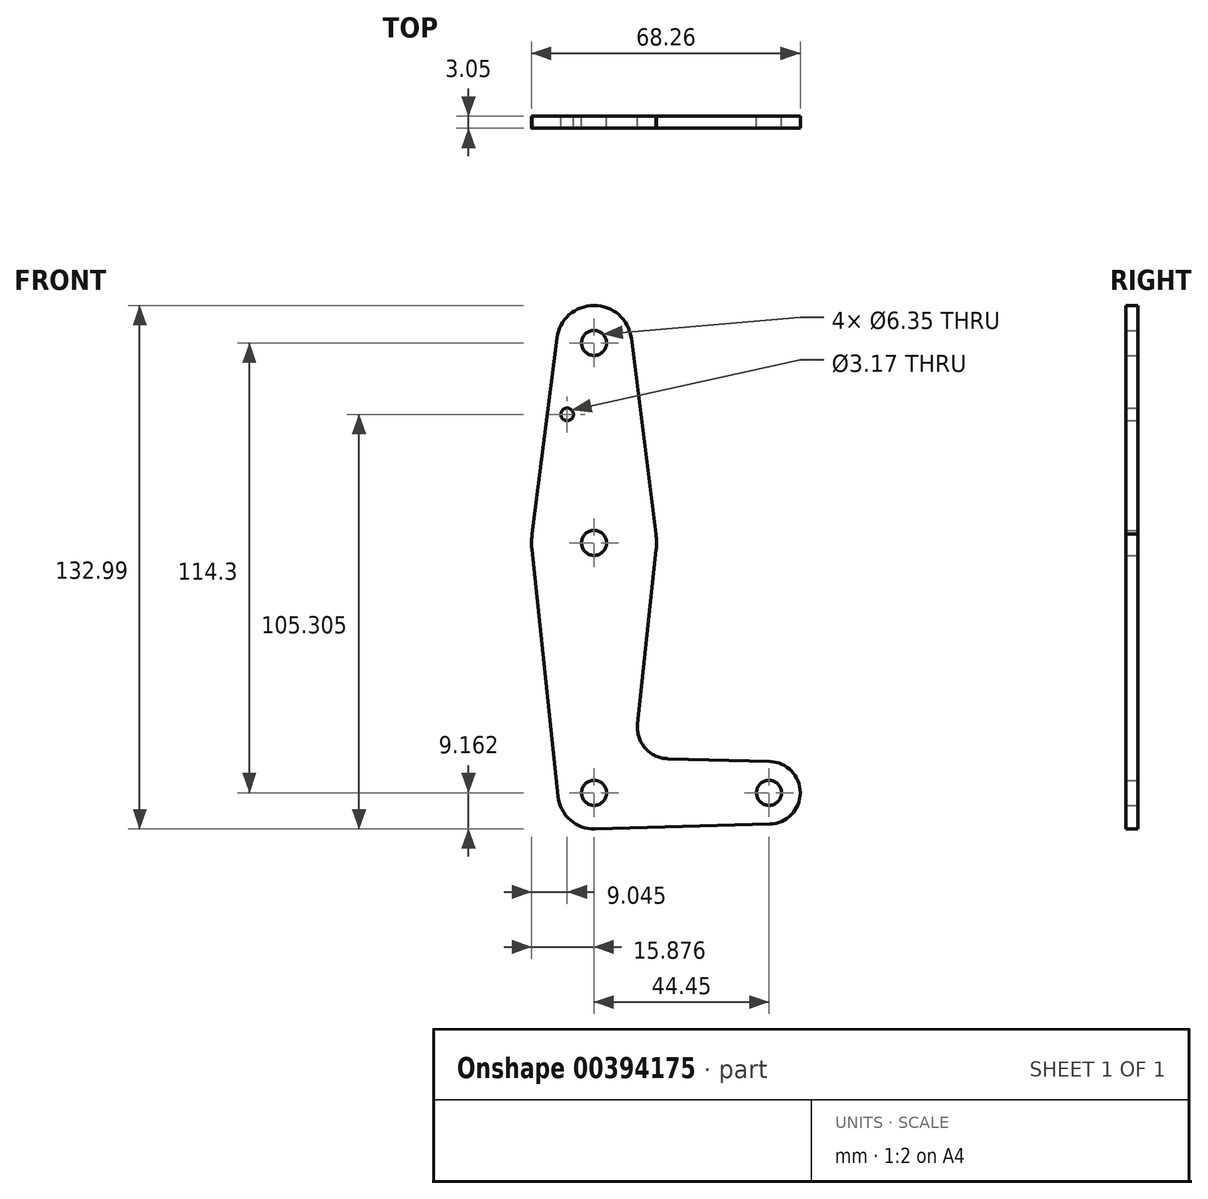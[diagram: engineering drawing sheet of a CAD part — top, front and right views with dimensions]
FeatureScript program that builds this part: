
annotation { "Feature Type Name" : "Feature", "Feature Type Description" : "" }
export const myFeature = defineFeature(function(context is Context, id is Id, definition is map)
    precondition{}
    {
        {
            var Q0;
            Q0=qCreatedBy(makeId("Front.planeOp"),FACE);
            var sketch = newSketch(context, id + "F0", { "sketchPlane" : qUnion([Q0])});
            skLineSegment(sketch, "E0", {"start": v(-37.08, 62.07) * mm, "end": v(-37.08, -52.23) * mm, "construction": true});
            skLineSegment(sketch, "E1", {"start": v(-37.08, -52.23) * mm, "end": v(7.37, -52.23) * mm, "construction": true});
            skCircle(sketch, "E2", {"center": v(-37.08, 62.07) * mm, "radius": 9.53 * mm});
            skCircle(sketch, "E3", {"center": v(-37.08, 11.27) * mm, "radius": 15.88 * mm});
            skCircle(sketch, "E4", {"center": v(-37.08, -52.23) * mm, "radius": 9.17 * mm});
            skCircle(sketch, "E5", {"center": v(7.37, -52.23) * mm, "radius": 7.94 * mm});
            skLineSegment(sketch, "E6", {"start": v(-52.87, 12.92) * mm, "end": v(-46.53, 63.26) * mm});
            skLineSegment(sketch, "E7", {"start": v(-27.63, 63.26) * mm, "end": v(-21.3, 12.92) * mm});
            skLineSegment(sketch, "E8", {"start": v(-52.87, 9.63) * mm, "end": v(-46.2, -53.2) * mm});
            skLineSegment(sketch, "E9", {"start": v(-26.01, -34.8) * mm, "end": v(-21.3, 9.63) * mm});
            skLineSegment(sketch, "E10", {"start": v(7.59, -44.3) * mm, "end": v(-18.33, -43.58) * mm});
            skLineSegment(sketch, "E11", {"start": v(-36.83, -61.4) * mm, "end": v(7.59, -60.16) * mm});
            skCircle(sketch, "E12", {"center": v(-37.08, 62.07) * mm, "radius": 3.18 * mm});
            skCircle(sketch, "E13", {"center": v(-37.08, 11.27) * mm, "radius": 3.18 * mm});
            skCircle(sketch, "E14", {"center": v(-37.08, -52.23) * mm, "radius": 3.18 * mm});
            skCircle(sketch, "E15", {"center": v(7.37, -52.23) * mm, "radius": 3.18 * mm});
            skCircle(sketch, "E16", {"center": v(-43.92, 43.92) * mm, "radius": 1.59 * mm});
            skPoint(sketch, "E17.newPointA", {"position": v(-27.97, -53.2) * mm});
            skPoint(sketch, "E17.newPointB", {"position": v(-36.83, -43.07) * mm});
            skArc(sketch, "E17.filletArc", {"start": v(-26.01, -34.8) * mm, "mid": v(-24.1, -40.86) * mm, "end": v(-18.33, -43.58) * mm});
            skSolve(sketch);
        }
        {
            var Q0;
            Q0 = qSketchRegion(id + "F0", true);
            extrude(context, id + "F1", {"entities" : qUnion([Q0]), "depth" : 3.05 * mm});
        }
    });
